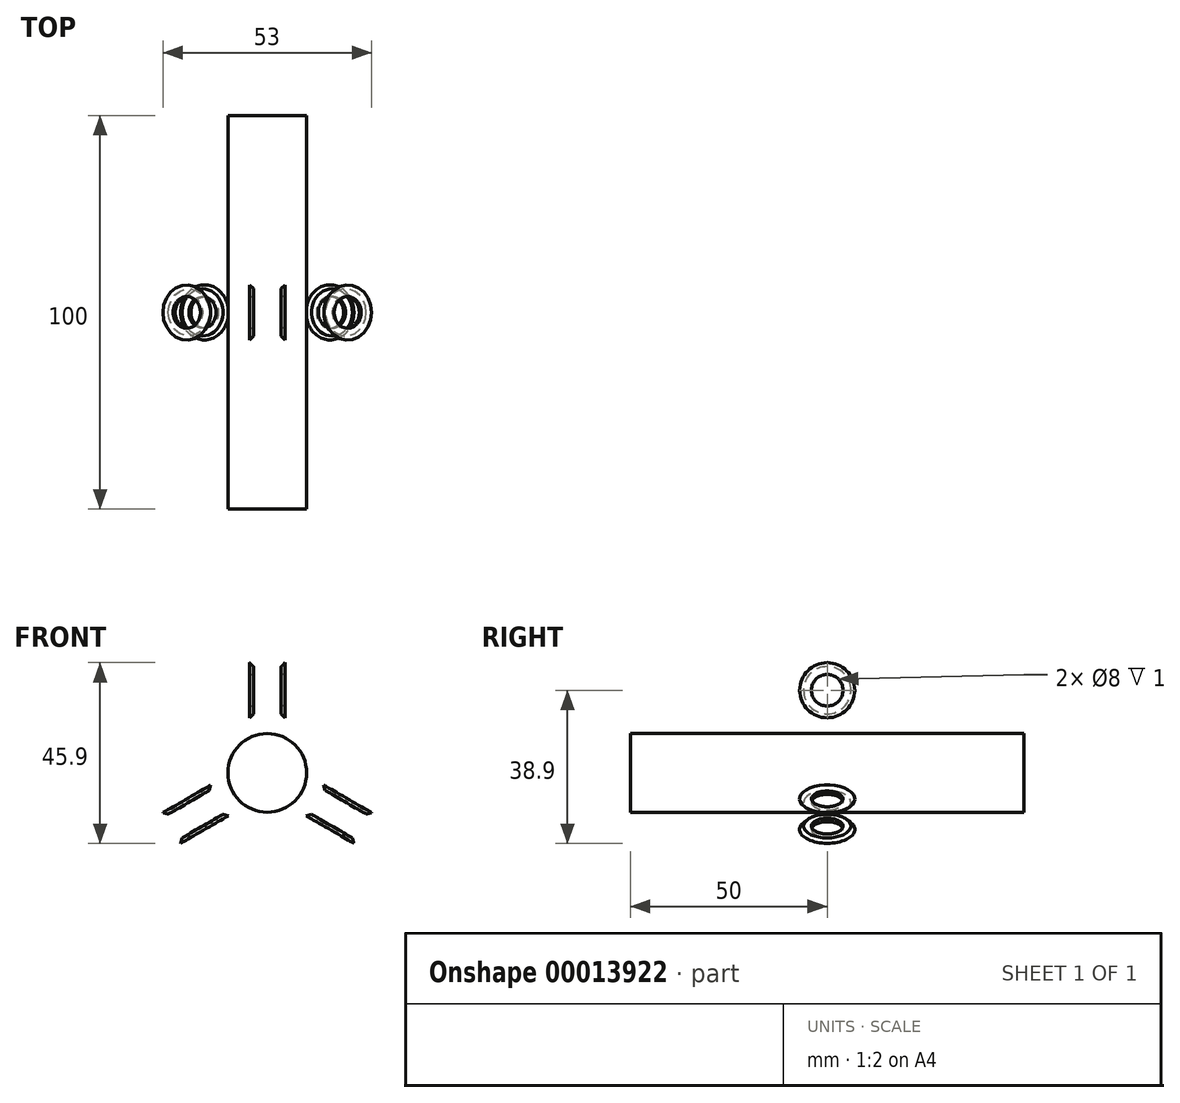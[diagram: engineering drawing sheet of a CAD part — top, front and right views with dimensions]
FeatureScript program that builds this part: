
annotation { "Feature Type Name" : "Feature", "Feature Type Description" : "" }
export const myFeature = defineFeature(function(context is Context, id is Id, definition is map)
    precondition{}
    {
        {
            var Q0;
            Q0=qCreatedBy(makeId("Front.planeOp"),FACE);
            var sketch = newSketch(context, id + "F0", { "sketchPlane" : qUnion([Q0])});
            skCircle(sketch, "E0", {"center": v(-45.2, 0) * mm, "radius": 10 * mm});
            skLineSegment(sketch, "E1.bottom", {"start": v(-48.7, 32) * mm, "end": v(-41.7, 32) * mm, "construction": true});
            skLineSegment(sketch, "E1.top", {"start": v(-48.7, 10) * mm, "end": v(-41.7, 10) * mm, "construction": true});
            skLineSegment(sketch, "E1.left", {"start": v(-48.7, 32) * mm, "end": v(-48.7, 10) * mm, "construction": true});
            skLineSegment(sketch, "E1.right", {"start": v(-41.7, 32) * mm, "end": v(-41.7, 10) * mm, "construction": true});
            skPoint(sketch, "E2", {"position": v(-45.2, 10) * mm});
            skLineSegment(sketch, "E3", {"start": v(-45.2, 0) * mm, "end": v(-45.2, 10) * mm, "construction": true});
            skPoint(sketch, "E4", {"position": v(-48.7, 21) * mm});
            skPoint(sketch, "E5", {"position": v(-41.7, 21) * mm});
            skLineSegment(sketch, "E6", {"start": v(-48.7, 25) * mm, "end": v(-41.7, 25) * mm, "construction": true});
            skLineSegment(sketch, "E7", {"start": v(-41.7, 17) * mm, "end": v(-48.7, 17) * mm, "construction": true});
            skLineSegment(sketch, "E8", {"start": v(-48.7, 21) * mm, "end": v(-41.7, 21) * mm, "construction": true});
            skLineSegment(sketch, "E9", {"start": v(-41.7, 27) * mm, "end": v(-41.7, 15) * mm});
            skLineSegment(sketch, "E10.MirrorCS", {"start": v(-48.7, 27) * mm, "end": v(-48.7, 15) * mm});
            skLineSegment(sketch, "E11", {"start": v(-41.7, 27) * mm, "end": v(-40.7, 28) * mm});
            skLineSegment(sketch, "E12.MirrorCS", {"start": v(-41.7, 15) * mm, "end": v(-40.7, 14) * mm});
            skLineSegment(sketch, "E13.MirrorCS", {"start": v(-48.7, 15) * mm, "end": v(-49.7, 14) * mm});
            skLineSegment(sketch, "E14.MirrorCS", {"start": v(-48.7, 27) * mm, "end": v(-49.7, 28) * mm});
            skLineSegment(sketch, "E15.1.0", {"start": v(-71.16, -19.03) * mm, "end": v(-52.1, -8.03) * mm, "construction": true});
            skLineSegment(sketch, "E15.1.1", {"start": v(-71.16, -19.03) * mm, "end": v(-74.66, -12.97) * mm, "construction": true});
            skLineSegment(sketch, "E15.1.2", {"start": v(-74.66, -12.97) * mm, "end": v(-55.6, -1.97) * mm, "construction": true});
            skLineSegment(sketch, "E15.1.3", {"start": v(-52.1, -8.03) * mm, "end": v(-55.6, -1.97) * mm, "construction": true});
            skLineSegment(sketch, "E15.2.0", {"start": v(-15.73, -12.97) * mm, "end": v(-34.78, -1.97) * mm, "construction": true});
            skLineSegment(sketch, "E15.2.1", {"start": v(-15.73, -12.97) * mm, "end": v(-19.23, -19.03) * mm, "construction": true});
            skLineSegment(sketch, "E15.2.2", {"start": v(-19.23, -19.03) * mm, "end": v(-38.28, -8.03) * mm, "construction": true});
            skLineSegment(sketch, "E15.2.3", {"start": v(-34.78, -1.97) * mm, "end": v(-38.28, -8.03) * mm, "construction": true});
            skLineSegment(sketch, "E16", {"start": v(-40.7, 28) * mm, "end": v(-40.7, 25) * mm});
            skLineSegment(sketch, "E17", {"start": v(-40.7, 25) * mm, "end": v(-41.7, 25) * mm});
            skSolve(sketch);
        }
        {
            var Q0;
            Q0=makeQuery(id+"F0.imprint","IMPRINT",FACE,{"disambiguationData":[TD([[makeQuery(id+"F0.imprint","IMPRINT",EDGE,{"derivedFrom":sQuery(id+"F0.wireOp",EDGE,"E0")}),1.0]])]});
            extrude(context, id + "F1", {"entities" : qUnion([Q0]), "endBound" : BoundingType.SYMMETRIC, "depth" : 100 * mm});
        }
        {
            var Q0;
            {var subQ0=sQuery(id+"F0.wireOp",EDGE,"E11");Q0=makeQuery(id+"F0.imprint","IMPRINT",FACE,{"disambiguationData":[TD([[makeQuery(id+"F0.imprint","IMPRINT",EDGE,{"derivedFrom":subQ0}),-1.0]])]});}
            var Q1;
            Q1=sQuery(id+"F0.wireOp",EDGE,"E8");
            revolve(context, id + "F2", {"entities" : qUnion([Q0]), "axis" : qUnion([Q1]), "revolveType" : RevolveType.FULL});
        }
        {
            var Q0;
            Q0=qCreatedBy(makeId("Right.planeOp"),FACE);
            var Q1;
            Q1=sQuery(id+"F0.wireOp",VERTEX,"E2");
            cPlane(context, id + "F3", {"entities" : qUnion([Q0, Q1]), "cplaneType" : CPlaneType.PLANE_POINT, "offset" : 150 * mm, "width" : 150 * mm, "height" : 150 * mm});
        }
        {
            var Q0;
            Q0=makeQuery(id+"F2.opRevolve","SWEPT_BODY",BODY,{"disambiguationData":[OSD([sQuery(id+"F0.wireOp",EDGE,"E9"),sQuery(id+"F0.wireOp",EDGE,"E11"),sQuery(id+"F0.wireOp",EDGE,"E16"),sQuery(id+"F0.wireOp",EDGE,"E17")])]});
            var Q1;
            Q1=qCreatedBy(id+"F3.planeOp",FACE);
            mirror(context, id + "F4", {"entities" : qUnion([Q0]), "mirrorPlane" : qUnion([Q1])});
        }
        {
            var Q0;
            Q0=qCreatedBy(makeId("Top.planeOp"),FACE);
            var sketch = newSketch(context, id + "F5", { "sketchPlane" : qUnion([Q0])});
            skLineSegment(sketch, "E18.0", {"start": v(-35.2, 50) * mm, "end": v(-55.2, 50) * mm});
            skLineSegment(sketch, "E19.0", {"start": v(-35.2, -50) * mm, "end": v(-55.2, -50) * mm});
            skLineSegment(sketch, "E20", {"start": v(-45.2, 50) * mm, "end": v(-45.2, -50) * mm, "construction": true});
            skSolve(sketch);
        }
        {
            var Q0;
            Q0=makeQuery(id+"F4.opPattern","COPY",BODY,{"derivedFrom":makeQuery(id+"F2.opRevolve","SWEPT_BODY",BODY,{"disambiguationData":[OSD([sQuery(id+"F0.wireOp",EDGE,"E9"),sQuery(id+"F0.wireOp",EDGE,"E11"),sQuery(id+"F0.wireOp",EDGE,"E16"),sQuery(id+"F0.wireOp",EDGE,"E17")])]}),"instanceName":"1"});
            var Q1;
            Q1=makeQuery(id+"F2.opRevolve","SWEPT_BODY",BODY,{"disambiguationData":[OSD([sQuery(id+"F0.wireOp",EDGE,"E9"),sQuery(id+"F0.wireOp",EDGE,"E11"),sQuery(id+"F0.wireOp",EDGE,"E16"),sQuery(id+"F0.wireOp",EDGE,"E17")])]});
            var Q2;
            Q2=sQuery(id+"F5.wireOp",EDGE,"E20");
            circularPattern(context, id + "F6", {"entities" : qUnion([Q0, Q1]), "axis" : qUnion([Q2]), "angle" : 120 * degree, "instanceCount" : 3});
        }
    });
